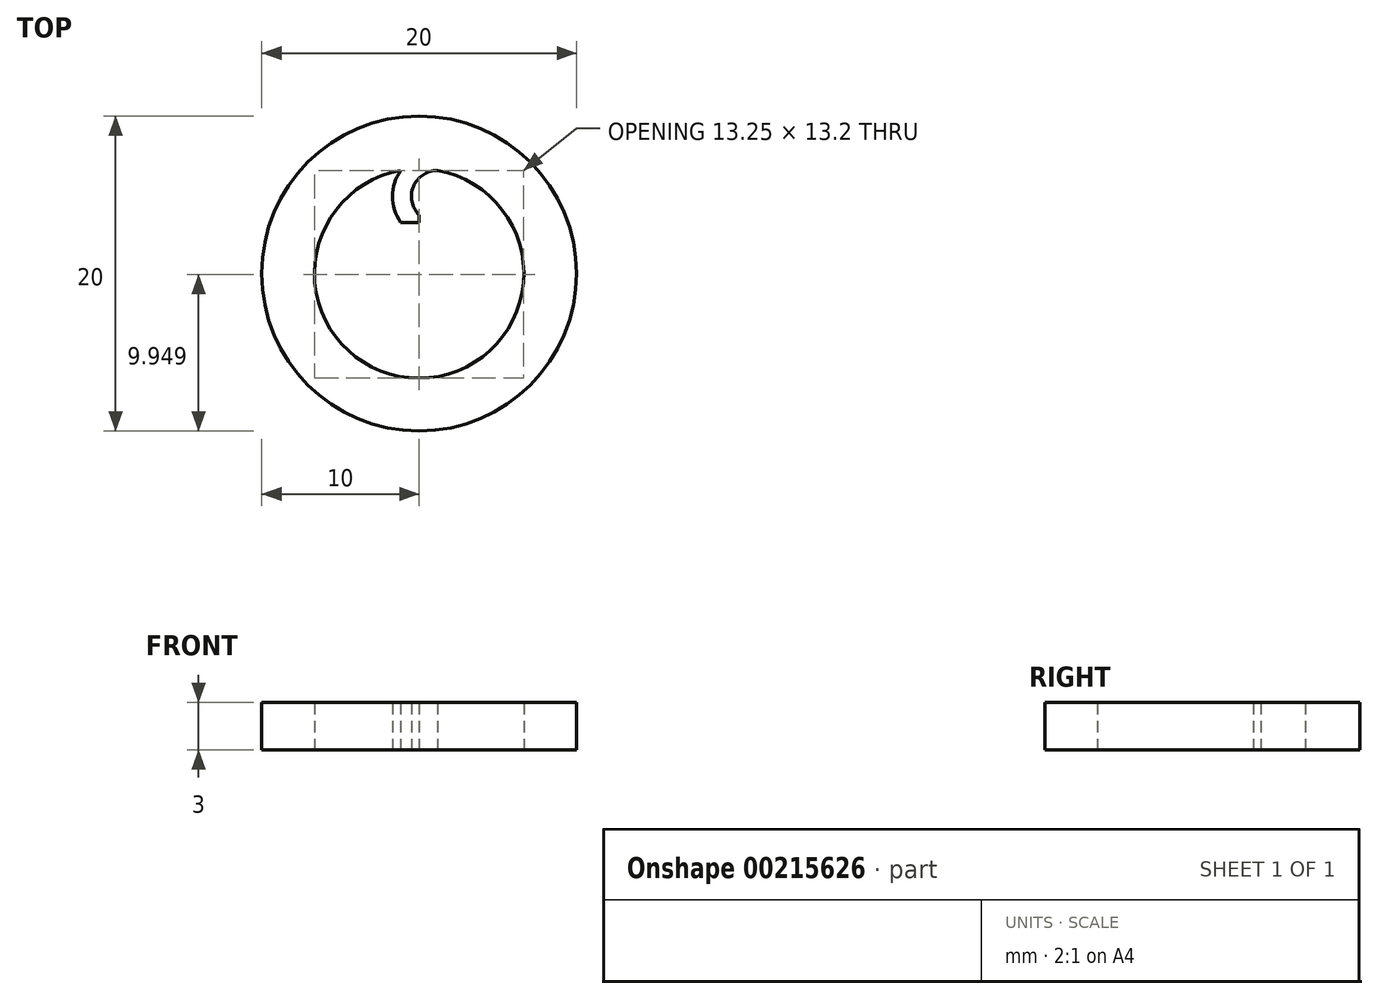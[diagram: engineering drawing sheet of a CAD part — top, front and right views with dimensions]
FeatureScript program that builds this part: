
annotation { "Feature Type Name" : "Feature", "Feature Type Description" : "" }
export const myFeature = defineFeature(function(context is Context, id is Id, definition is map)
    precondition{}
    {
        {
            var Q0;
            Q0=qCreatedBy(makeId("Top.planeOp"),FACE);
            var sketch = newSketch(context, id + "F0", { "sketchPlane" : qUnion([Q0])});
            skCircle(sketch, "E0", {"center": v(0, 0) * mm, "radius": 6.65 * mm});
            skCircle(sketch, "E1", {"center": v(0, 0) * mm, "radius": 10 * mm});
            skSolve(sketch);
        }
        {
            var Q0;
            Q0=qSketchRegion(id+"F0",true);
            extrude(context, id + "F1", {"entities" : qUnion([Q0]), "depth" : 3 * mm});
        }
        {
            var Q0;
            Q0=qCreatedBy(makeId("Top.planeOp"),FACE);
            var sketch = newSketch(context, id + "F2", { "sketchPlane" : qUnion([Q0])});
            skCircle(sketch, "E2.0", {"center": v(0, 0) * mm, "radius": 6.65 * mm});
            skLineSegment(sketch, "E3", {"start": v(-1.16, 3.25) * mm, "end": v(1.16, 3.25) * mm});
            skLineSegment(sketch, "E4", {"start": v(1.16, 3.25) * mm, "end": v(1.16, 6.55) * mm, "construction": true});
            skLineSegment(sketch, "E5", {"start": v(0, 0) * mm, "end": v(0, 3.25) * mm, "construction": true});
            skArc(sketch, "E6", {"start": v(1.16, 6.55) * mm, "mid": v(-0.49, 4.9) * mm, "end": v(1.16, 3.25) * mm});
            skArc(sketch, "E7", {"start": v(1.16, 7.75) * mm, "mid": v(-1.69, 4.9) * mm, "end": v(1.16, 2.05) * mm});
            skLineSegment(sketch, "E8", {"start": v(0, 3.25) * mm, "end": v(0, 3.73) * mm});
            skSolve(sketch);
        }
        {
            var Q0;
            {var subQ0=sQuery(id+"F2.wireOp",EDGE,"N0US4zlP-Tiaw-jmlp-6OOO-6123ut0QMheT");Q0=makeQuery(id+"F2.imprint","IMPRINT",FACE,{"disambiguationData":[TD([[makeQuery(id+"F2.imprint","IMPRINT",EDGE,{"derivedFrom":subQ0}),1.0]])]});}
            var Q1;
            {var subQ7=sQuery(id+"F2.wireOp",EDGE,"E8");Q1=makeQuery(id+"F2.imprint","IMPRINT",FACE,{"disambiguationData":[TD([[makeQuery(id+"F2.imprint","IMPRINT",EDGE,{"derivedFrom":subQ7}),1.0]])]});}
            var Q2;
            Q2=makeQuery(id+"F1.opExtrude","CAP_FACE",FACE,{"disambiguationData":[OSD([sQuery(id+"F0.wireOp",EDGE,"E0"),sQuery(id+"F0.wireOp",EDGE,"E1")])],"isStart":false});
            extrude(context, id + "F3", {"entities" : qUnion([Q0, Q1]), "operationType" : NewBodyOperationType.ADD, "endBound" : BoundingType.UP_TO_SURFACE, "endBoundEntityFace" : qUnion([Q2]), "depth" : 5 * mm});
        }
    });
